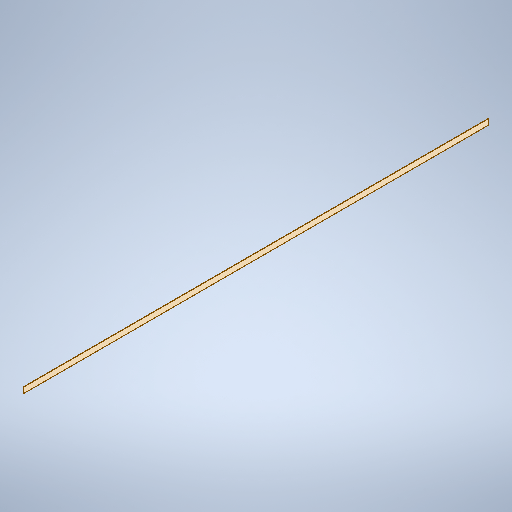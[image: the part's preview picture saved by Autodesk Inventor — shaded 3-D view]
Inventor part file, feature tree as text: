
AUTODESK INVENTOR PART (.ipt)
format: ipt  version: 2025 (Build 290162010, 162A)  size: 252,928 bytes
history: native  units: in
note: dims shown in document units (in); Inventor stores cm internally (conversion verified against a paired STEP export)
features: extrude x1, sketch x1
ambient origin geometry x8: Origin, YZ Plane, XZ Plane, XY Plane, X Axis, Y Axis, Z Axis, Center Point
bodies: Solid1 (feature_tree)
feature tree (2):
  extrude  "Extrusion1"  Depth=3.5in
  sketch  "Sketch1"  dims[d0=0.25in d1=3.5in d2=288.0in d3=0.0in]
